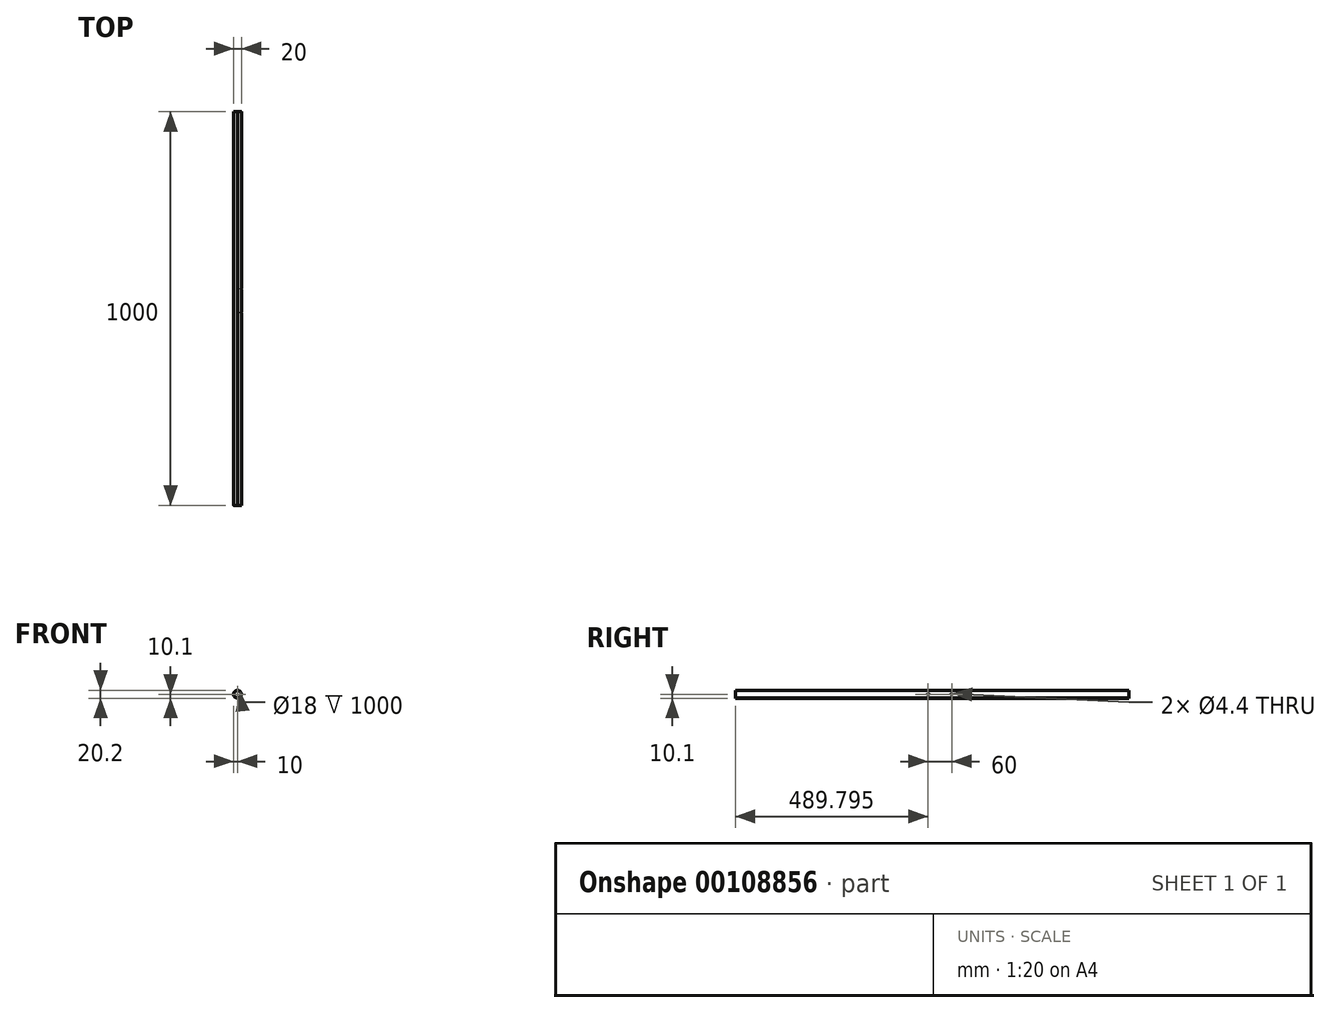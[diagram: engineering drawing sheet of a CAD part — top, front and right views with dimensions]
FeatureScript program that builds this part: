
annotation { "Feature Type Name" : "Feature", "Feature Type Description" : "" }
export const myFeature = defineFeature(function(context is Context, id is Id, definition is map)
    precondition{}
    {
        {
            var Q0;
            Q0=qCreatedBy(makeId("Front.planeOp"),FACE);
            var sketch = newSketch(context, id + "F0", { "sketchPlane" : qUnion([Q0])});
            skArc(sketch, "E0", {"start": v(-0.3, 10) * mm, "mid": v(-10, 0) * mm, "end": v(-0.3, -10) * mm});
            skCircle(sketch, "E1", {"center": v(0, 0) * mm, "radius": 9 * mm});
            skLineSegment(sketch, "E2", {"start": v(-24.1, 0) * mm, "end": v(36.83, 0) * mm, "construction": true});
            skLineSegment(sketch, "E3", {"start": v(0, 26.87) * mm, "end": v(0, -23.65) * mm, "construction": true});
            skLineSegment(sketch, "E4", {"start": v(-0.3, -10) * mm, "end": v(-0.3, -10.1) * mm});
            skLineSegment(sketch, "E5", {"start": v(-0.3, -10.1) * mm, "end": v(0.3, -10.1) * mm});
            skLineSegment(sketch, "E6", {"start": v(0.3, -10.1) * mm, "end": v(0.3, -10) * mm});
            skLineSegment(sketch, "E7", {"start": v(0, -10) * mm, "end": v(6.49, -10) * mm, "construction": true});
            skLineSegment(sketch, "E8.MirrorCS", {"start": v(-0.3, 10) * mm, "end": v(-0.3, 10.1) * mm});
            skLineSegment(sketch, "E9.MirrorCS", {"start": v(0.3, 10.1) * mm, "end": v(0.3, 10) * mm});
            skLineSegment(sketch, "E10.MirrorCS", {"start": v(-0.3, 10.1) * mm, "end": v(0.3, 10.1) * mm});
            skArc(sketch, "E11.trimOffspring", {"start": v(0.3, -10) * mm, "mid": v(10, 0) * mm, "end": v(0.3, 10) * mm});
            skSolve(sketch);
        }
        {
            var Q0;
            Q0=makeQuery(id+"F0.imprint","IMPRINT",FACE,{"disambiguationData":[TD([[makeQuery(id+"F0.imprint","IMPRINT",EDGE,{"derivedFrom":sQuery(id+"F0.wireOp",EDGE,"E0")}),1.0]])]});
            var Q1;
            Q1=sQuery(id+"F0.wireOp",EDGE,"E1");
            var Q2;
            Q2=sQuery(id+"F0.wireOp",EDGE,"E0");
            extrude(context, id + "F1", {"entities" : qUnion([Q0]), "surfaceEntities" : qUnion([Q1, Q2]), "depth" : 1000 * mm});
        }
        {
            var Q0;
            Q0=qCreatedBy(makeId("Right.planeOp"),FACE);
            var sketch = newSketch(context, id + "F2", { "sketchPlane" : qUnion([Q0])});
            skLineSegment(sketch, "E12", {"start": v(47.64, 0) * mm, "end": v(-1009.74, 0) * mm, "construction": true});
            skLineSegment(sketch, "E13", {"start": v(-980.2, -16.32) * mm, "end": v(-980.2, 44.8) * mm, "construction": true});
            skLineSegment(sketch, "E14", {"start": v(0, -10.7) * mm, "end": v(0, 37.1) * mm, "construction": true});
            skLineSegment(sketch, "E15", {"start": v(-510.2, 76.76) * mm, "end": v(-510.2, -85.46) * mm, "construction": true});
            skLineSegment(sketch, "E16", {"start": v(-450.2, 80.42) * mm, "end": v(-450.2, -107.42) * mm, "construction": true});
            skPoint(sketch, "E17", {"position": v(-510.2, 0) * mm});
            skPoint(sketch, "E18", {"position": v(-450.2, 0) * mm});
            skSolve(sketch);
        }
        {
            var Q0;
            Q0=sQuery(id+"F2.wireOp",VERTEX,"E17");
            var Q1;
            Q1=sQuery(id+"F2.wireOp",VERTEX,"E18");
            var Q2;
            Q2=makeQuery(id+"F1.opExtrude","SWEPT_BODY",BODY,{"disambiguationData":[OSD([sQuery(id+"F0.wireOp",EDGE,"E0"),sQuery(id+"F0.wireOp",EDGE,"E1")])]});
            hole(context, id + "F3", {"style" : HoleStyle.SIMPLE, "endStyle" : HoleEndStyle.THROUGH, "oppositeDirection" : true, "standardTappedOrClearance" : lookupTablePath({ "standard" : "ISO", "fit" : "Normal", "size" : "M4", "type" : "Clearance" }), "standardBlindInLast" : lookupTablePath({ "fit" : "Standard", "standard" : "ISO", "size" : "M4", "type" : "Clearance" }), "holeDiameter" : 4.4 * mm, "startFromSketch" : true, "locations" : qUnion([Q0, Q1]), "scope" : qUnion([Q2]), "isTappedThrough" : true});
        }
    });
